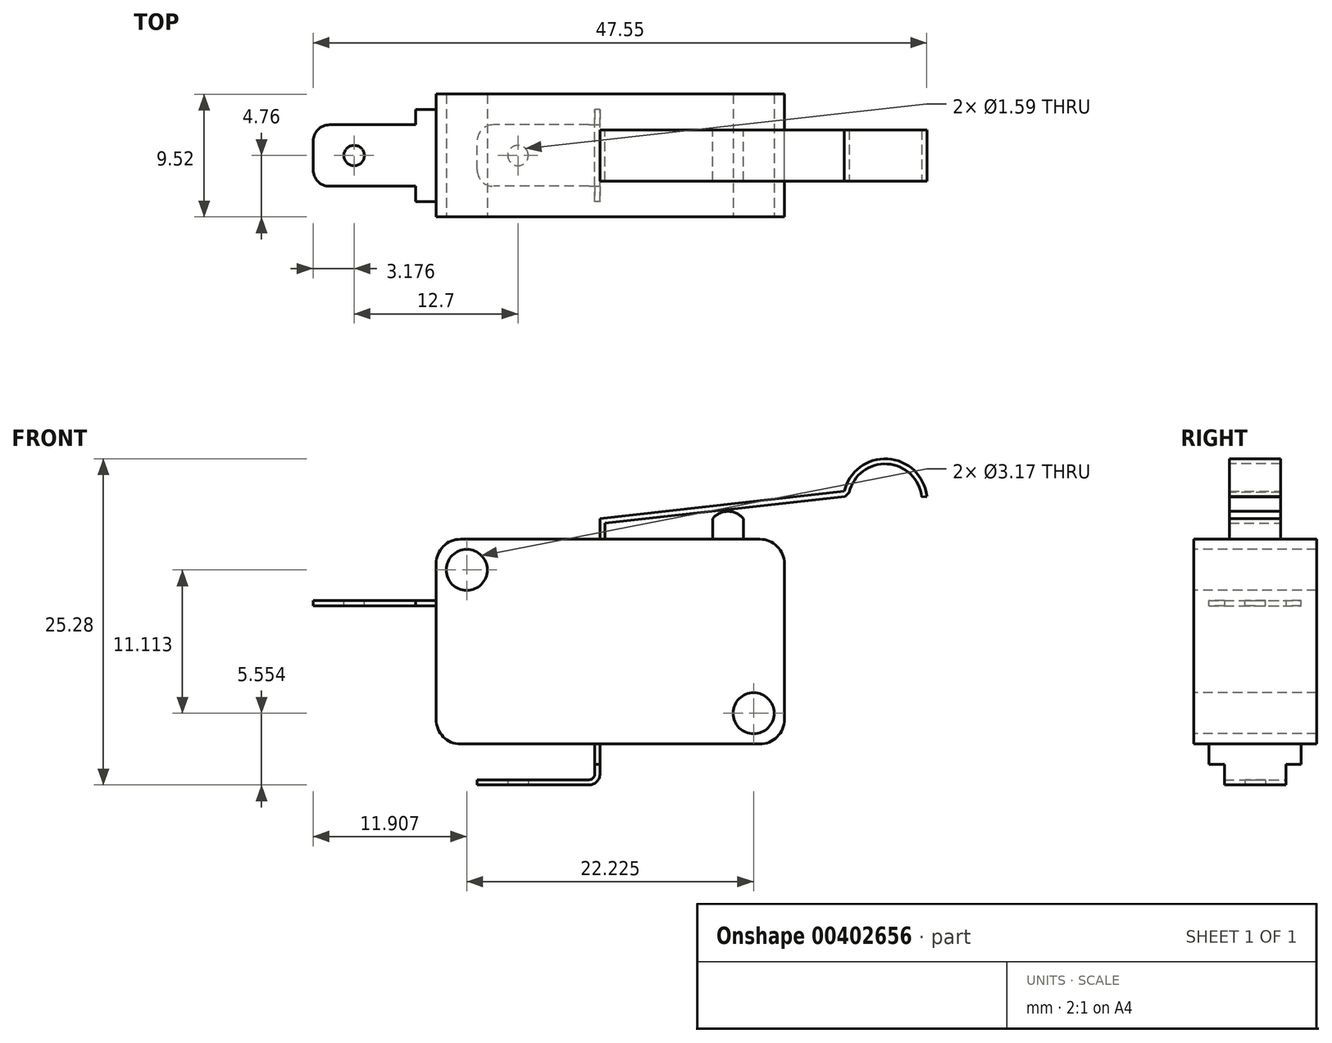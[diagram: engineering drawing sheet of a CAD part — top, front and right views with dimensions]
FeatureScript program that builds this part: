
annotation { "Feature Type Name" : "Feature", "Feature Type Description" : "" }
export const myFeature = defineFeature(function(context is Context, id is Id, definition is map)
    precondition{}
    {
        {
            var Q0;
            Q0=qCreatedBy(makeId("Front.planeOp"),FACE);
            var sketch = newSketch(context, id + "F0", { "sketchPlane" : qUnion([Q0])});
            skLineSegment(sketch, "E0.bottom", {"start": v(13.5, 7.94) * mm, "end": v(-13.5, 7.94) * mm});
            skLineSegment(sketch, "E0.top", {"start": v(13.5, -7.94) * mm, "end": v(-13.5, -7.94) * mm});
            skLineSegment(sketch, "E0.left", {"start": v(13.5, 7.94) * mm, "end": v(13.5, -7.94) * mm});
            skLineSegment(sketch, "E0.right", {"start": v(-13.5, 7.94) * mm, "end": v(-13.5, -7.94) * mm});
            skPoint(sketch, "E0.middle", {"position": v(0, 0) * mm});
            skSolve(sketch);
        }
        {
            var Q0;
            Q0=qSketchRegion(id+"F0",true);
            extrude(context, id + "F1", {"entities" : qUnion([Q0]), "depth" : 9.52 * mm, "symmetric" : true});
        }
        {
            var Q0;
            Q0=qCreatedBy(makeId("Front.planeOp"),FACE);
            var sketch = newSketch(context, id + "F2", { "sketchPlane" : qUnion([Q0])});
            skLineSegment(sketch, "E1.0", {"start": v(13.5, 7.94) * mm, "end": v(-13.5, 7.94) * mm, "construction": true});
            skLineSegment(sketch, "E2", {"start": v(-0.8, 7.94) * mm, "end": v(-0.8, 9.53) * mm});
            skLineSegment(sketch, "E3", {"start": v(-0.8, 9.53) * mm, "end": v(18.14, 11.65) * mm});
            skLineSegment(sketch, "E4", {"start": v(18.14, 11.65) * mm, "end": v(18.18, 11.26) * mm});
            skLineSegment(sketch, "E5", {"start": v(18.18, 11.26) * mm, "end": v(-0.4, 9.17) * mm});
            skLineSegment(sketch, "E6", {"start": v(-0.4, 9.17) * mm, "end": v(-0.4, 7.94) * mm});
            skLineSegment(sketch, "E7", {"start": v(-0.4, 7.94) * mm, "end": v(-0.8, 7.94) * mm});
            skSolve(sketch);
        }
        {
            var Q0;
            Q0=qSketchRegion(id+"F2",true);
            extrude(context, id + "F3", {"entities" : qUnion([Q0]), "operationType" : NewBodyOperationType.ADD, "depth" : 3.97 * mm, "symmetric" : true});
        }
        {
            var Q0;
            Q0=makeQuery(id+"F3.opExtrude","CAP_FACE",FACE,{"disambiguationData":[OSD([sQuery(id+"F2.wireOp",EDGE,"E2"),sQuery(id+"F2.wireOp",EDGE,"E3"),sQuery(id+"F2.wireOp",EDGE,"E4"),sQuery(id+"F2.wireOp",EDGE,"E5"),sQuery(id+"F2.wireOp",EDGE,"E6"),sQuery(id+"F2.wireOp",EDGE,"E7")])],"isStart":false});
            var sketch = newSketch(context, id + "F4", { "sketchPlane" : qUnion([Q0])});
            skArc(sketch, "E8", {"start": v(24.53, 11.26) * mm, "mid": v(21.5, 14.17) * mm, "end": v(18.14, 11.65) * mm});
            skLineSegment(sketch, "E9", {"start": v(18.18, 11.26) * mm, "end": v(27.02, 11.26) * mm, "construction": true});
            skArc(sketch, "E10.0", {"start": v(24.14, 11.22) * mm, "mid": v(21.48, 13.77) * mm, "end": v(18.52, 11.57) * mm});
            skLineSegment(sketch, "E11", {"start": v(18.52, 11.57) * mm, "end": v(18.18, 11.26) * mm});
            skLineSegment(sketch, "E12", {"start": v(18.18, 11.26) * mm, "end": v(18.14, 11.65) * mm});
            skLineSegment(sketch, "E13", {"start": v(24.14, 11.22) * mm, "end": v(24.53, 11.26) * mm});
            skSolve(sketch);
        }
        {
            var Q0;
            Q0=qSketchRegion(id+"F4",true);
            var Q1;
            Q1=makeQuery(id+"F3.opExtrude","CAP_FACE",FACE,{"disambiguationData":[OSD([sQuery(id+"F2.wireOp",EDGE,"E2"),sQuery(id+"F2.wireOp",EDGE,"E3"),sQuery(id+"F2.wireOp",EDGE,"E4"),sQuery(id+"F2.wireOp",EDGE,"E5"),sQuery(id+"F2.wireOp",EDGE,"E6"),sQuery(id+"F2.wireOp",EDGE,"E7")])],"isStart":true});
            extrude(context, id + "F5", {"entities" : qUnion([Q0]), "operationType" : NewBodyOperationType.ADD, "endBound" : BoundingType.UP_TO_SURFACE, "oppositeDirection" : true, "endBoundEntityFace" : qUnion([Q1]), "depth" : 25.4 * mm});
        }
        {
            var Q0;
            Q0=qCreatedBy(makeId("Front.planeOp"),FACE);
            var sketch = newSketch(context, id + "F6", { "sketchPlane" : qUnion([Q0])});
            skLineSegment(sketch, "E14.0", {"start": v(13.5, 7.94) * mm, "end": v(-13.5, 7.94) * mm, "construction": true});
            skLineSegment(sketch, "E15.bottom", {"start": v(10.32, 7.94) * mm, "end": v(7.94, 7.94) * mm});
            skLineSegment(sketch, "E15.left", {"start": v(10.32, 7.94) * mm, "end": v(10.32, 9.53) * mm});
            skLineSegment(sketch, "E15.right", {"start": v(7.94, 7.94) * mm, "end": v(7.94, 9.53) * mm});
            skArc(sketch, "E16", {"start": v(10.32, 9.53) * mm, "mid": v(9.13, 10.1) * mm, "end": v(7.94, 9.53) * mm});
            skSolve(sketch);
        }
        {
            var Q0;
            Q0=qSketchRegion(id+"F6",true);
            extrude(context, id + "F7", {"entities" : qUnion([Q0]), "operationType" : NewBodyOperationType.ADD, "depth" : 3.97 * mm, "symmetric" : true});
        }
        {
            var Q0;
            Q0=qCreatedBy(makeId("Front.planeOp"),FACE);
            var sketch = newSketch(context, id + "F8", { "sketchPlane" : qUnion([Q0])});
            skLineSegment(sketch, "E17.0", {"start": v(-13.5, 7.94) * mm, "end": v(-13.5, -7.94) * mm, "construction": true});
            skLineSegment(sketch, "E18.bottom", {"start": v(-13.5, 3.18) * mm, "end": v(-23.02, 3.18) * mm});
            skLineSegment(sketch, "E18.top", {"start": v(-13.5, 2.78) * mm, "end": v(-23.02, 2.78) * mm});
            skLineSegment(sketch, "E18.left", {"start": v(-13.5, 3.18) * mm, "end": v(-13.5, 2.78) * mm});
            skLineSegment(sketch, "E18.right", {"start": v(-23.02, 3.18) * mm, "end": v(-23.02, 2.78) * mm});
            skSolve(sketch);
        }
        {
            var Q0;
            Q0=qSketchRegion(id+"F8",true);
            extrude(context, id + "F9", {"entities" : qUnion([Q0]), "operationType" : NewBodyOperationType.ADD, "depth" : 4.76 * mm, "symmetric" : true});
        }
        {
            var Q0;
            Q0=makeQuery(id+"F9.opExtrude","SWEPT_FACE",FACE,{"disambiguationData":[OSD([sQuery(id+"F8.wireOp",EDGE,"E18.bottom")])]});
            var sketch = newSketch(context, id + "F10", { "sketchPlane" : qUnion([Q0])});
            skLineSegment(sketch, "E19.0", {"start": v(-13.5, -4.76) * mm, "end": v(-13.5, 4.76) * mm, "construction": true});
            skLineSegment(sketch, "E20.bottom", {"start": v(-13.5, 3.57) * mm, "end": v(-15.08, 3.57) * mm});
            skLineSegment(sketch, "E20.top", {"start": v(-13.5, -3.57) * mm, "end": v(-15.08, -3.57) * mm});
            skLineSegment(sketch, "E20.left", {"start": v(-13.5, 3.57) * mm, "end": v(-13.5, -3.57) * mm});
            skLineSegment(sketch, "E20.right", {"start": v(-15.08, 3.57) * mm, "end": v(-15.08, -3.57) * mm});
            skSolve(sketch);
        }
        {
            var Q0;
            Q0=qSketchRegion(id+"F10",true);
            var Q1;
            Q1=makeQuery(id+"F9.opExtrude","SWEPT_FACE",FACE,{"disambiguationData":[OSD([sQuery(id+"F8.wireOp",EDGE,"E18.top")])]});
            extrude(context, id + "F11", {"entities" : qUnion([Q0]), "operationType" : NewBodyOperationType.ADD, "endBound" : BoundingType.UP_TO_SURFACE, "oppositeDirection" : true, "endBoundEntityFace" : qUnion([Q1]), "depth" : 25.4 * mm});
        }
        {
            var Q0;
            Q0=makeQuery(id+"F11.boolean.opBoolean","MERGE",FACE,{"derivedFrom":[makeQuery(id+"F9.opExtrude","SWEPT_FACE",FACE,{"disambiguationData":[OSD([sQuery(id+"F8.wireOp",EDGE,"E18.bottom")])]}),makeQuery(id+"F11.opExtrude","CAP_FACE",FACE,{"disambiguationData":[OSD([sQuery(id+"F10.wireOp",EDGE,"E20.bottom"),sQuery(id+"F10.wireOp",EDGE,"E20.top"),sQuery(id+"F10.wireOp",EDGE,"E20.left"),sQuery(id+"F10.wireOp",EDGE,"E20.right")])],"isStart":true})]});
            var sketch = newSketch(context, id + "F12", { "sketchPlane" : qUnion([Q0])});
            skCircle(sketch, "E21", {"center": v(-19.84, 0) * mm, "radius": 0.8 * mm});
            skSolve(sketch);
        }
        {
            var Q0;
            Q0=qSketchRegion(id+"F12",true);
            extrude(context, id + "F13", {"entities" : qUnion([Q0]), "operationType" : NewBodyOperationType.REMOVE, "endBound" : BoundingType.THROUGH_ALL, "oppositeDirection" : true, "depth" : 25.4 * mm});
        }
        {
            var Q0;
            Q0=makeQuery(id+"F9.opExtrude","CAP_EDGE",EDGE,{"disambiguationData":[OSD([sQuery(id+"F8.wireOp",EDGE,"E18.right")])],"isStart":false});
            var Q1;
            Q1=makeQuery(id+"F9.opExtrude","CAP_EDGE",EDGE,{"disambiguationData":[OSD([sQuery(id+"F8.wireOp",EDGE,"E18.right")])],"isStart":true});
            fillet(context, id + "F14", {"entities" : qUnion([Q0, Q1]), "radius" : 1.27 * mm, "tangentPropagation" : true, "allowEdgeOverflow" : false});
        }
        {
            var Q0;
            Q0=qCreatedBy(makeId("Front.planeOp"),FACE);
            var sketch = newSketch(context, id + "F15", { "sketchPlane" : qUnion([Q0])});
            skLineSegment(sketch, "E22.0", {"start": v(-0.8, 7.94) * mm, "end": v(-0.8, 9.53) * mm, "construction": true});
            skLineSegment(sketch, "E23.0", {"start": v(13.5, -7.94) * mm, "end": v(-13.5, -7.94) * mm, "construction": true});
            skLineSegment(sketch, "E24", {"start": v(-0.8, -7.94) * mm, "end": v(-0.8, -10.25) * mm});
            skLineSegment(sketch, "E25", {"start": v(-1.66, -11.11) * mm, "end": v(-10.32, -11.11) * mm});
            skPoint(sketch, "E26.visualSharp", {"position": v(-0.8, -11.11) * mm});
            skArc(sketch, "E26.filletArc", {"start": v(-1.66, -11.11) * mm, "mid": v(-1.05, -10.86) * mm, "end": v(-0.8, -10.25) * mm});
            skLineSegment(sketch, "E27.0", {"start": v(-1.2, -7.94) * mm, "end": v(-1.2, -10.25) * mm});
            skArc(sketch, "E28.0", {"start": v(-1.66, -10.72) * mm, "mid": v(-1.33, -10.58) * mm, "end": v(-1.2, -10.25) * mm});
            skLineSegment(sketch, "E29.0", {"start": v(-1.66, -10.72) * mm, "end": v(-10.32, -10.72) * mm});
            skLineSegment(sketch, "E30", {"start": v(-10.32, -10.72) * mm, "end": v(-10.32, -11.11) * mm});
            skLineSegment(sketch, "E31", {"start": v(-1.2, -7.94) * mm, "end": v(-0.8, -7.94) * mm});
            skSolve(sketch);
        }
        {
            var Q0;
            Q0=qSketchRegion(id+"F15",true);
            extrude(context, id + "F16", {"entities" : qUnion([Q0]), "operationType" : NewBodyOperationType.ADD, "depth" : 4.76 * mm, "symmetric" : true});
        }
        {
            var Q0;
            Q0=makeQuery(id+"F16.opExtrude","SWEPT_FACE",FACE,{"disambiguationData":[OSD([sQuery(id+"F15.wireOp",EDGE,"E27.0")])]});
            var sketch = newSketch(context, id + "F17", { "sketchPlane" : qUnion([Q0])});
            skLineSegment(sketch, "E32.0", {"start": v(4.76, -7.94) * mm, "end": v(-4.76, -7.94) * mm, "construction": true});
            skLineSegment(sketch, "E33.bottom", {"start": v(-3.57, -7.94) * mm, "end": v(3.57, -7.94) * mm});
            skLineSegment(sketch, "E33.top", {"start": v(-3.57, -9.52) * mm, "end": v(3.57, -9.52) * mm});
            skLineSegment(sketch, "E33.left", {"start": v(-3.57, -7.94) * mm, "end": v(-3.57, -9.52) * mm});
            skLineSegment(sketch, "E33.right", {"start": v(3.57, -7.94) * mm, "end": v(3.57, -9.52) * mm});
            skSolve(sketch);
        }
        {
            var Q0;
            Q0=qSketchRegion(id+"F17",true);
            var Q1;
            Q1=makeQuery(id+"F16.opExtrude","SWEPT_FACE",FACE,{"disambiguationData":[OSD([sQuery(id+"F15.wireOp",EDGE,"E24")])]});
            extrude(context, id + "F18", {"entities" : qUnion([Q0]), "operationType" : NewBodyOperationType.ADD, "endBound" : BoundingType.UP_TO_SURFACE, "oppositeDirection" : true, "endBoundEntityFace" : qUnion([Q1]), "depth" : 25.4 * mm});
        }
        {
            var Q0;
            Q0=makeQuery(id+"F16.opExtrude","SWEPT_FACE",FACE,{"disambiguationData":[OSD([sQuery(id+"F15.wireOp",EDGE,"E25")])]});
            var sketch = newSketch(context, id + "F19", { "sketchPlane" : qUnion([Q0])});
            skCircle(sketch, "E34", {"center": v(-7.14, 0) * mm, "radius": 0.8 * mm});
            skLineSegment(sketch, "E35.0", {"start": v(-0.8, 2.38) * mm, "end": v(-0.8, -2.38) * mm, "construction": true});
            skSolve(sketch);
        }
        {
            var Q0;
            Q0=qSketchRegion(id+"F19",true);
            extrude(context, id + "F20", {"entities" : qUnion([Q0]), "operationType" : NewBodyOperationType.REMOVE, "endBound" : BoundingType.UP_TO_NEXT, "oppositeDirection" : true, "depth" : 25.4 * mm});
        }
        {
            var Q0;
            Q0=makeQuery(id+"F16.opExtrude","CAP_EDGE",EDGE,{"disambiguationData":[OSD([sQuery(id+"F15.wireOp",EDGE,"E30")])],"isStart":true});
            var Q1;
            Q1=makeQuery(id+"F16.opExtrude","CAP_EDGE",EDGE,{"disambiguationData":[OSD([sQuery(id+"F15.wireOp",EDGE,"E30")])],"isStart":false});
            fillet(context, id + "F21", {"entities" : qUnion([Q0, Q1]), "radius" : 1.27 * mm, "tangentPropagation" : true, "allowEdgeOverflow" : false});
        }
        {
            var Q0;
            Q0=makeQuery(id+"F1.opExtrude","CAP_FACE",FACE,{"disambiguationData":[OSD([sQuery(id+"F0.wireOp",EDGE,"E0.bottom"),sQuery(id+"F0.wireOp",EDGE,"E0.top"),sQuery(id+"F0.wireOp",EDGE,"E0.left"),sQuery(id+"F0.wireOp",EDGE,"E0.right")])],"isStart":false});
            var sketch = newSketch(context, id + "F22", { "sketchPlane" : qUnion([Q0])});
            skCircle(sketch, "E36", {"center": v(-11.11, 5.56) * mm, "radius": 1.59 * mm});
            skSolve(sketch);
        }
        {
            var Q0;
            Q0=qSketchRegion(id+"F22",true);
            extrude(context, id + "F23", {"entities" : qUnion([Q0]), "operationType" : NewBodyOperationType.REMOVE, "endBound" : BoundingType.THROUGH_ALL, "oppositeDirection" : true, "depth" : 25.4 * mm});
        }
        {
            var Q0;
            Q0=makeQuery(id+"F1.opExtrude","CAP_FACE",FACE,{"disambiguationData":[OSD([sQuery(id+"F0.wireOp",EDGE,"E0.bottom"),sQuery(id+"F0.wireOp",EDGE,"E0.top"),sQuery(id+"F0.wireOp",EDGE,"E0.left"),sQuery(id+"F0.wireOp",EDGE,"E0.right")])],"isStart":false});
            var sketch = newSketch(context, id + "F24", { "sketchPlane" : qUnion([Q0])});
            skCircle(sketch, "E37", {"center": v(11.11, -5.56) * mm, "radius": 1.59 * mm});
            skSolve(sketch);
        }
        {
            var Q0;
            Q0=qSketchRegion(id+"F24",true);
            extrude(context, id + "F25", {"entities" : qUnion([Q0]), "operationType" : NewBodyOperationType.REMOVE, "endBound" : BoundingType.THROUGH_ALL, "oppositeDirection" : true, "depth" : 25.4 * mm});
        }
        {
            var Q0;
            Q0=makeQuery(id+"F1.opExtrude","SWEPT_EDGE",EDGE,{"disambiguationData":[OSD([sQuery(id+"F0.wireOp",EDGE,"E0.bottom"),sQuery(id+"F0.wireOp",EDGE,"E0.right")])]});
            var Q1;
            Q1=makeQuery(id+"F1.opExtrude","SWEPT_EDGE",EDGE,{"disambiguationData":[OSD([sQuery(id+"F0.wireOp",EDGE,"E0.bottom"),sQuery(id+"F0.wireOp",EDGE,"E0.left")])]});
            var Q2;
            Q2=makeQuery(id+"F1.opExtrude","SWEPT_EDGE",EDGE,{"disambiguationData":[OSD([sQuery(id+"F0.wireOp",EDGE,"E0.top"),sQuery(id+"F0.wireOp",EDGE,"E0.left")])]});
            var Q3;
            Q3=makeQuery(id+"F1.opExtrude","SWEPT_EDGE",EDGE,{"disambiguationData":[OSD([sQuery(id+"F0.wireOp",EDGE,"E0.top"),sQuery(id+"F0.wireOp",EDGE,"E0.right")])]});
            fillet(context, id + "F26", {"entities" : qUnion([Q0, Q1, Q2, Q3]), "radius" : 1.9 * mm, "tangentPropagation" : true, "allowEdgeOverflow" : false});
        }
    });
